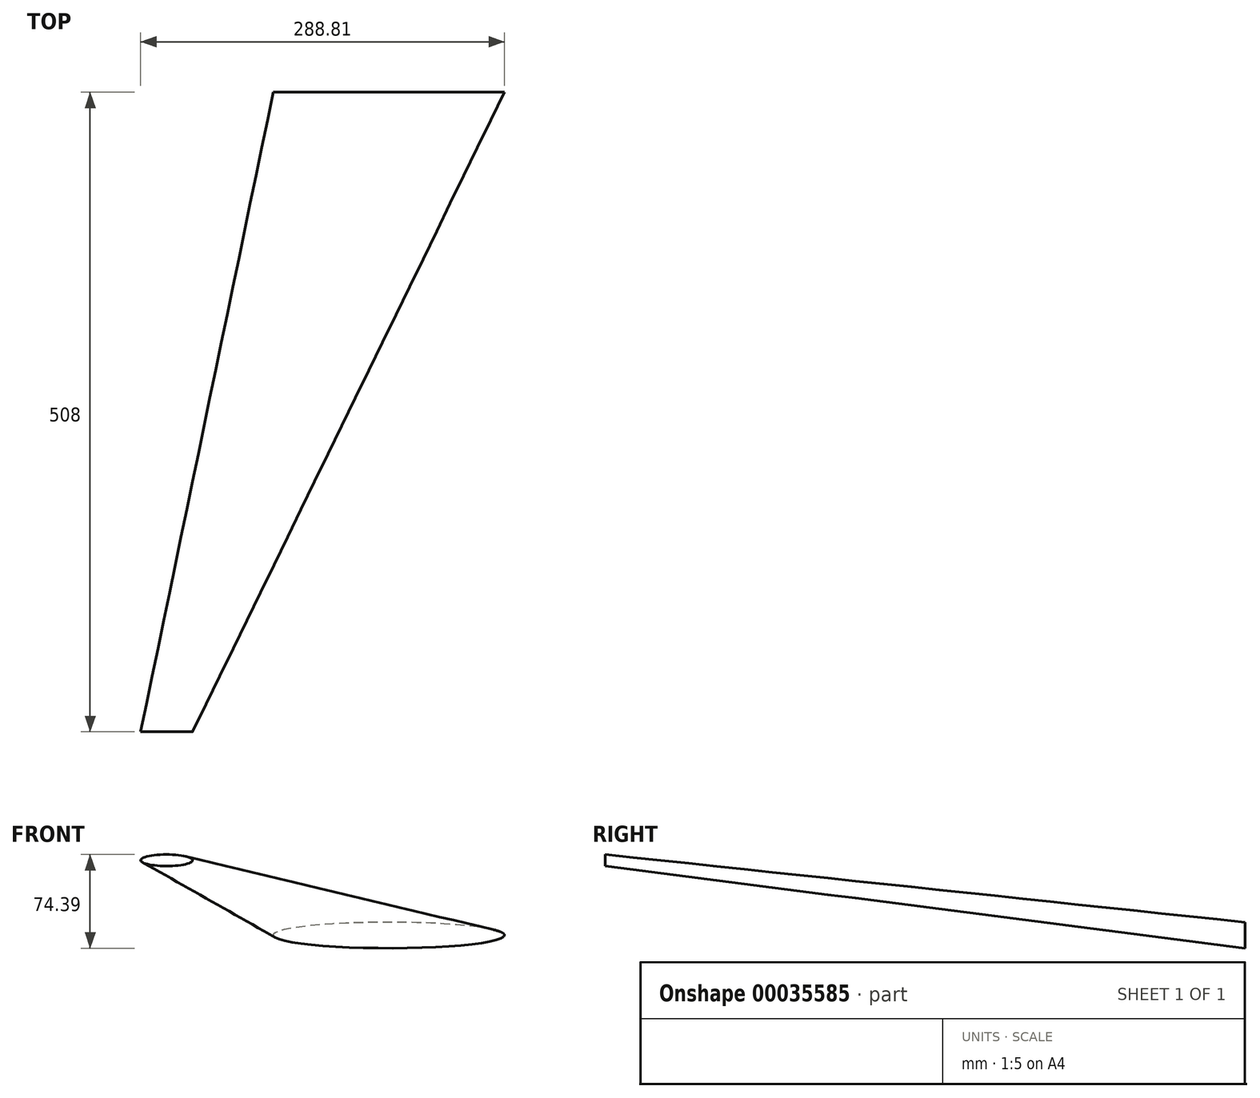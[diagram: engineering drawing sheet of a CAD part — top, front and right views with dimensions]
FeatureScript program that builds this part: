
annotation { "Feature Type Name" : "Feature", "Feature Type Description" : "" }
export const myFeature = defineFeature(function(context is Context, id is Id, definition is map)
    precondition{}
    {
        {
            var Q0;
            Q0=qCreatedBy(makeId("Front.planeOp"),FACE);
            var sketch = newSketch(context, id + "F0", { "sketchPlane" : qUnion([Q0])});
            skEllipse(sketch, "E0", {"center": v(0, 0) * mm, "majorRadius": 91.77 * mm, "minorRadius": 10.31 * mm, "majorAxis": v(1, 0)});
            skSolve(sketch);
        }
        {
            var Q0;
            Q0=qCreatedBy(makeId("Front.planeOp"),FACE);
            cPlane(context, id + "F1", {"entities" : qUnion([Q0]), "cplaneType" : CPlaneType.OFFSET, "offset" : 508 * mm, "width" : 152.4 * mm, "height" : 152.4 * mm});
        }
        {
            var Q0;
            Q0=qCreatedBy(id+"F1.planeOp",FACE);
            var sketch = newSketch(context, id + "F2", { "sketchPlane" : qUnion([Q0])});
            skEllipse(sketch, "E1", {"center": v(-176.43, 59.5) * mm, "majorRadius": 20.6 * mm, "minorRadius": 4.57 * mm, "majorAxis": v(1, 0)});
            skSolve(sketch);
        }
        {
            var Q0;
            Q0=makeQuery(id+"F0.imprint","IMPRINT",FACE,{"disambiguationData":[TD([[makeQuery(id+"F0.imprint","IMPRINT",EDGE,{"derivedFrom":sQuery(id+"F0.wireOp",EDGE,"E0")}),1.0]])]});
            var Q1;
            Q1=makeQuery(id+"F2.imprint","IMPRINT",FACE,{"disambiguationData":[TD([[makeQuery(id+"F2.imprint","IMPRINT",EDGE,{"derivedFrom":sQuery(id+"F2.wireOp",EDGE,"E1")}),1.0]])]});
            loft(context, id + "F3", {"sheetProfilesArray" : [{ "sheetProfileEntities" : qUnion([Q0]) }, { "sheetProfileEntities" : qUnion([Q1]) }]});
        }
    });
